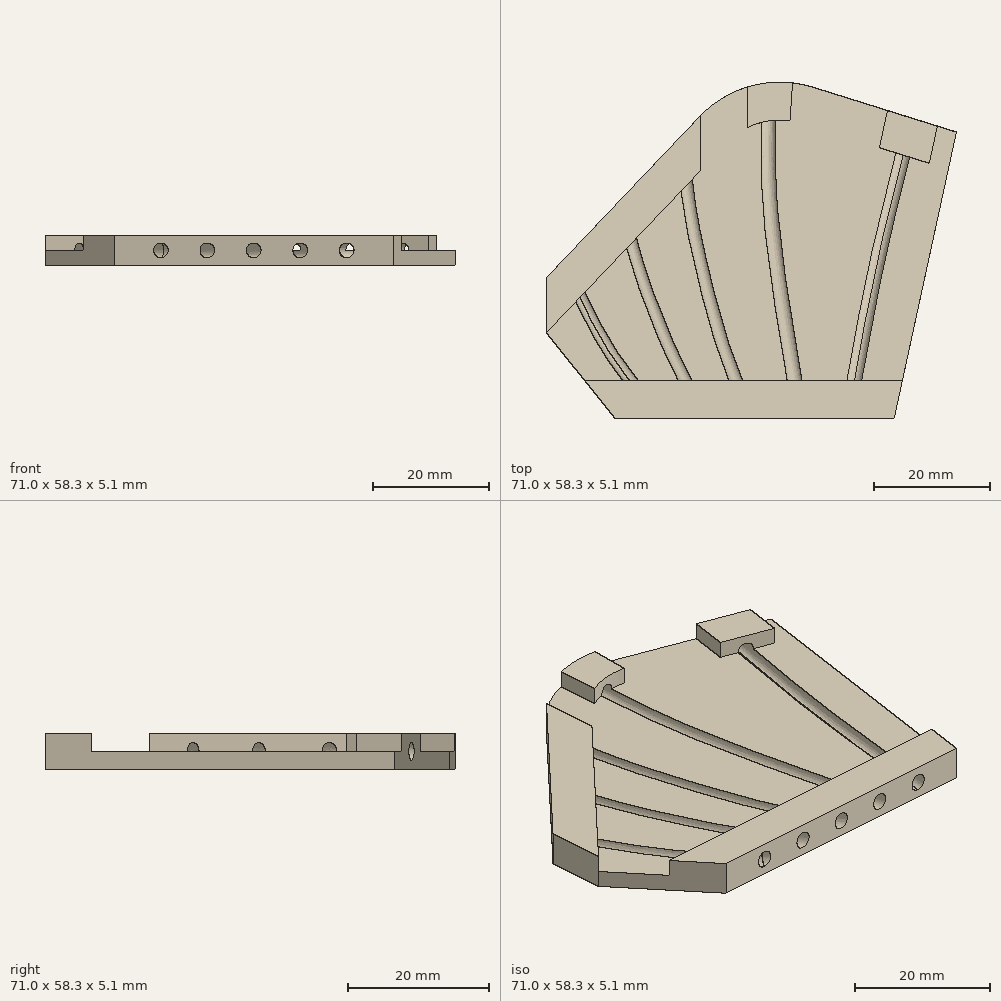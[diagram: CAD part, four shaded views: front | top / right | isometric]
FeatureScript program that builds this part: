
annotation { "Feature Type Name" : "Feature", "Feature Type Description" : "" }
export const myFeature = defineFeature(function(context is Context, id is Id, definition is map)
    precondition{}
    {
        {
            var Q0;
            Q0=qCreatedBy(makeId("Top.planeOp"),FACE);
            var sketch = newSketch(context, id + "F0", { "sketchPlane" : qUnion([Q0])});
            skLineSegment(sketch, "E0", {"start": v(0, 0) * mm, "end": v(48.26, 0) * mm});
            skSolve(sketch);
        }
        {
            var Q0;
            Q0=qCreatedBy(makeId("Top.planeOp"),FACE);
            var sketch = newSketch(context, id + "F1", { "sketchPlane" : qUnion([Q0])});
            skLineSegment(sketch, "E1", {"start": v(0, 0) * mm, "end": v(48.26, 0) * mm});
            skLineSegment(sketch, "E2", {"start": v(48.26, 0) * mm, "end": v(59.06, 49.64) * mm});
            skLineSegment(sketch, "E3", {"start": v(0, 0) * mm, "end": v(-11.94, 14.85) * mm});
            skLineSegment(sketch, "E4", {"start": v(-11.94, 14.85) * mm, "end": v(-11.94, 24.37) * mm});
            skLineSegment(sketch, "E5", {"start": v(-11.94, 24.37) * mm, "end": v(14.69, 52.37) * mm});
            skLineSegment(sketch, "E6", {"start": v(34.18, 57.42) * mm, "end": v(59.06, 49.64) * mm});
            skPoint(sketch, "E7.visualSharp", {"position": v(22.86, 60.96) * mm});
            skArc(sketch, "E7.filletArc", {"start": v(34.18, 57.42) * mm, "mid": v(23.71, 57.68) * mm, "end": v(14.69, 52.37) * mm});
            skSolve(sketch);
        }
        {
            var Q0;
            Q0 = qSketchRegion(id + "F1", true);
            extrude(context, id + "F2", {"entities" : qUnion([Q0]), "depth" : 2.54 * mm, "offsetDistance" : 25.4 * mm});
        }
        {
            var Q0;
            Q0=makeQuery(id+"F2.opExtrude","CAP_FACE",FACE,{"disambiguationData":[OSD([sQuery(id+"F1.wireOp",EDGE,"E1"),sQuery(id+"F1.wireOp",EDGE,"E2"),sQuery(id+"F1.wireOp",EDGE,"E3"),sQuery(id+"F1.wireOp",EDGE,"E4"),sQuery(id+"F1.wireOp",EDGE,"E5"),sQuery(id+"F1.wireOp",EDGE,"E6"),sQuery(id+"F1.wireOp",EDGE,"E7.filletArc")])],"isStart":false});
            var sketch = newSketch(context, id + "F3", { "sketchPlane" : qUnion([Q0])});
            skLineSegment(sketch, "E8", {"start": v(-11.94, 14.85) * mm, "end": v(14.69, 42.84) * mm});
            skLineSegment(sketch, "E9", {"start": v(14.69, 52.37) * mm, "end": v(14.69, 42.84) * mm});
            skLineSegment(sketch, "E10", {"start": v(49.69, 6.56) * mm, "end": v(-5.28, 6.56) * mm});
            skLineSegment(sketch, "E11.0", {"start": v(45.72, 46.93) * mm, "end": v(54.36, 44.23) * mm});
            skArc(sketch, "E11.1", {"start": v(30.23, 51.6) * mm, "mid": v(26.45, 51.56) * mm, "end": v(22.85, 50.38) * mm});
            skLineSegment(sketch, "E12", {"start": v(30.23, 51.6) * mm, "end": v(30.67, 58.16) * mm});
            skLineSegment(sketch, "E13", {"start": v(22.85, 50.38) * mm, "end": v(22.85, 57.44) * mm});
            skLineSegment(sketch, "E14", {"start": v(55.76, 50.67) * mm, "end": v(54.36, 44.23) * mm});
            skLineSegment(sketch, "E15", {"start": v(47.12, 53.37) * mm, "end": v(45.72, 46.93) * mm});
            skSolve(sketch);
        }
        {
            var Q0;
            Q0 = qSketchRegion(id + "F3", true);
            var Q1;
            Q1=makeQuery(id+"F3.imprint","IMPRINT",FACE,{"disambiguationData":[TD([[makeQuery(id+"F3.imprint","IMPRINT",EDGE,{"derivedFrom":sQuery(id+"F3.wireOp",EDGE,"E8")}),1.0]])]});
            var Q2;
            Q2=makeQuery(id+"F3.imprint","IMPRINT",FACE,{"disambiguationData":[TD([[makeQuery(id+"F3.imprint","IMPRINT",EDGE,{"derivedFrom":sQuery(id+"F3.wireOp",EDGE,"E11.1")}),-1.0]])]});
            var Q3;
            Q3=makeQuery(id+"F3.imprint","IMPRINT",FACE,{"disambiguationData":[TD([[makeQuery(id+"F3.imprint","IMPRINT",EDGE,{"derivedFrom":sQuery(id+"F3.wireOp",EDGE,"E11.0")}),1.0]])]});
            var Q4;
            {var subQ0=sQuery(id+"F3.wireOp",EDGE,"E10");Q4=makeQuery(id+"F3.imprint","IMPRINT",FACE,{"disambiguationData":[TD([[makeQuery(id+"F3.imprint","IMPRINT",EDGE,{"derivedFrom":subQ0}),1.0]])]});}
            extrude(context, id + "F4", {"entities" : qUnion([Q0, Q1, Q2, Q3, Q4]), "operationType" : NewBodyOperationType.ADD, "depth" : 2.54 * mm, "offsetDistance" : 25.4 * mm});
        }
        {
            var Q0;
            Q0=makeQuery(id+"F2.opExtrude","CAP_FACE",FACE,{"disambiguationData":[OSD([sQuery(id+"F1.wireOp",EDGE,"E1"),sQuery(id+"F1.wireOp",EDGE,"E2"),sQuery(id+"F1.wireOp",EDGE,"E3"),sQuery(id+"F1.wireOp",EDGE,"E4"),sQuery(id+"F1.wireOp",EDGE,"E5"),sQuery(id+"F1.wireOp",EDGE,"E6"),sQuery(id+"F1.wireOp",EDGE,"E7.filletArc")])],"isStart":false});
            var sketch = newSketch(context, id + "F5", { "sketchPlane" : qUnion([Q0])});
            skPoint(sketch, "E16", {"position": v(8.04, 0) * mm});
            skPoint(sketch, "E17.1.0.0", {"position": v(16.09, 0) * mm});
            skPoint(sketch, "E17.2.0.0", {"position": v(24.13, 0) * mm});
            skPoint(sketch, "E17.3.0.0", {"position": v(32.17, 0) * mm});
            skPoint(sketch, "E17.4.0.0", {"position": v(40.22, 0) * mm});
            skLineSegment(sketch, "E17.direction1", {"start": v(8.04, 0) * mm, "end": v(16.09, 0) * mm, "construction": true});
            skPoint(sketch, "E18", {"position": v(51.44, 52.02) * mm});
            skPoint(sketch, "E19.visualSharp", {"position": v(22.86, 60.96) * mm});
            skPoint(sketch, "E20", {"position": v(26.72, 58.2) * mm});
            skLineSegment(sketch, "E21", {"start": v(14.69, 52.37) * mm, "end": v(-11.94, 24.37) * mm});
            skPoint(sketch, "E22", {"position": v(1.37, 38.37) * mm});
            skPoint(sketch, "E23", {"position": v(11.88, 49.41) * mm});
            skPoint(sketch, "E24", {"position": v(-9.13, 27.33) * mm});
            skFitSpline(sketch, "E25", {"points": [v(51.44, 52.02) * mm, v(45.36, 27.29) * mm, v(40.22, 0) * mm], "startDerivative": vector(-13.01, -49.86) * mm, "endDerivative": vector(-9.46, -54.16) * mm});
            skFitSpline(sketch, "E26", {"points": [v(26.72, 58.2) * mm, v(26.72, 37.31) * mm, v(32.17, 0) * mm], "startDerivative": vector(-2.03, -45.53) * mm, "endDerivative": vector(12.23, -69.7) * mm});
            skFitSpline(sketch, "E27", {"points": [v(11.88, 49.41) * mm, v(15.75, 22.82) * mm, v(24.13, 0) * mm], "startDerivative": vector(-0.7, -55.32) * mm, "endDerivative": vector(25.48, -43.38) * mm});
            skFitSpline(sketch, "E28", {"points": [v(1.37, 38.37) * mm, v(6.4, 19.33) * mm, v(16.09, 0) * mm], "startDerivative": vector(3.78, -39.84) * mm, "endDerivative": vector(25.36, -36.93) * mm});
            skFitSpline(sketch, "E29", {"points": [v(-9.13, 27.33) * mm, v(-1.03, 11.48) * mm, v(8.04, 0) * mm], "startDerivative": vector(14.48, -31.8) * mm, "endDerivative": vector(19.95, -22.7) * mm});
            skSolve(sketch);
        }
        {
            var Q0;
            {var subQ0=sQuery(id+"F1.wireOp",EDGE,"E1");Q0=makeQuery(id+"F4.boolean.opBoolean","MERGE",FACE,{"derivedFrom":[makeQuery(id+"F2.opExtrude","SWEPT_FACE",FACE,{"disambiguationData":[OSD([subQ0])]}),makeQuery(id+"F4.opExtrude","SWEPT_FACE",FACE,{"disambiguationData":[OSD([subQ0])]})]});}
            var sketch = newSketch(context, id + "F6", { "sketchPlane" : qUnion([Q0])});
            skCircle(sketch, "E30", {"center": v(8.04, 2.54) * mm, "radius": 1.27 * mm});
            skPoint(sketch, "E30.centerSnap0", {"position": v(0, 2.54) * mm});
            skCircle(sketch, "E31.1.0.0", {"center": v(16.09, 2.54) * mm, "radius": 1.27 * mm});
            skCircle(sketch, "E31.2.0.0", {"center": v(24.13, 2.54) * mm, "radius": 1.27 * mm});
            skCircle(sketch, "E31.3.0.0", {"center": v(32.17, 2.54) * mm, "radius": 1.27 * mm});
            skCircle(sketch, "E31.4.0.0", {"center": v(40.22, 2.54) * mm, "radius": 1.27 * mm});
            skLineSegment(sketch, "E31.direction1", {"start": v(8.04, 2.54) * mm, "end": v(16.09, 2.54) * mm, "construction": true});
            skSolve(sketch);
        }
        {
            var Q0;
            Q0=makeQuery(id+"F6.imprint","IMPRINT",FACE,{"disambiguationData":[TD([[makeQuery(id+"F6.imprint","IMPRINT",EDGE,{"derivedFrom":sQuery(id+"F6.wireOp",EDGE,"E31.4.0.0")}),1.0]])]});
            var Q1;
            Q1=sQuery(id+"F5.wireOp",EDGE,"E25");
            sweep(context, id + "F7", {"operationType" : NewBodyOperationType.REMOVE, "profiles" : qUnion([Q0]), "path" : qUnion([Q1])});
        }
        {
            var Q0;
            Q0=makeQuery(id+"F6.imprint","IMPRINT",FACE,{"disambiguationData":[TD([[makeQuery(id+"F6.imprint","IMPRINT",EDGE,{"derivedFrom":sQuery(id+"F6.wireOp",EDGE,"E31.3.0.0")}),1.0]])]});
            var Q1;
            Q1=sQuery(id+"F5.wireOp",EDGE,"E26");
            sweep(context, id + "F8", {"operationType" : NewBodyOperationType.REMOVE, "profiles" : qUnion([Q0]), "path" : qUnion([Q1])});
        }
        {
            var Q0;
            Q0=makeQuery(id+"F6.imprint","IMPRINT",FACE,{"disambiguationData":[TD([[makeQuery(id+"F6.imprint","IMPRINT",EDGE,{"derivedFrom":sQuery(id+"F6.wireOp",EDGE,"E31.2.0.0")}),1.0]])]});
            var Q1;
            Q1=sQuery(id+"F5.wireOp",EDGE,"E27");
            sweep(context, id + "F9", {"operationType" : NewBodyOperationType.REMOVE, "profiles" : qUnion([Q0]), "path" : qUnion([Q1])});
        }
        {
            var Q0;
            Q0=makeQuery(id+"F6.imprint","IMPRINT",FACE,{"disambiguationData":[TD([[makeQuery(id+"F6.imprint","IMPRINT",EDGE,{"derivedFrom":sQuery(id+"F6.wireOp",EDGE,"E31.1.0.0")}),1.0]])]});
            var Q1;
            Q1=sQuery(id+"F5.wireOp",EDGE,"E28");
            sweep(context, id + "F10", {"operationType" : NewBodyOperationType.REMOVE, "profiles" : qUnion([Q0]), "path" : qUnion([Q1])});
        }
        {
            var Q0;
            Q0=makeQuery(id+"F6.imprint","IMPRINT",FACE,{"disambiguationData":[TD([[makeQuery(id+"F6.imprint","IMPRINT",EDGE,{"derivedFrom":sQuery(id+"F6.wireOp",EDGE,"E30")}),1.0]])]});
            var Q1;
            Q1=sQuery(id+"F6.wireOp",EDGE,"E30");
            var Q2;
            Q2=sQuery(id+"F5.wireOp",EDGE,"E29");
            sweep(context, id + "F11", {"operationType" : NewBodyOperationType.REMOVE, "profiles" : qUnion([Q0]), "surfaceProfiles" : qUnion([Q1]), "path" : qUnion([Q2])});
        }
        {
            var Q0;
            {var subQ0=sQuery(id+"F1.wireOp",EDGE,"E5");Q0=makeQuery(id+"F4.boolean.opBoolean","MERGE",FACE,{"derivedFrom":[makeQuery(id+"F2.opExtrude","SWEPT_FACE",FACE,{"disambiguationData":[OSD([subQ0])]}),makeQuery(id+"F4.opExtrude","SWEPT_FACE",FACE,{"disambiguationData":[OSD([subQ0])]})]});}
            var sketch = newSketch(context, id + "F12", { "sketchPlane" : qUnion([Q0])});
            skCircle(sketch, "E32", {"center": v(-44, 2.54) * mm, "radius": 1.27 * mm});
            skCircle(sketch, "E33", {"center": v(-28.75, 2.54) * mm, "radius": 1.27 * mm});
            skCircle(sketch, "E34", {"center": v(-13.51, 2.54) * mm, "radius": 1.27 * mm});
            skSolve(sketch);
        }
        {
            var Q0;
            {var subQ1=sQuery(id+"F6.wireOp",EDGE,"E31.2.0.0");var subQ2=sQuery(id+"F1.wireOp",EDGE,"E5");var subQ3=makeQuery(id+"F4.boolean.opBoolean","MERGE",FACE,{"derivedFrom":[makeQuery(id+"F2.opExtrude","SWEPT_FACE",FACE,{"disambiguationData":[OSD([subQ2])]}),makeQuery(id+"F4.opExtrude","SWEPT_FACE",FACE,{"disambiguationData":[OSD([subQ2])]})]});var subQ5=makeQuery(id+"F9.boolean.opBoolean","INTERSECT",EDGE,{"derivedFrom":[subQ3,makeQuery(id+"F9.opSweep","CAP_FACE",FACE,{"disambiguationData":[OSD([sQuery(id+"F5.wireOp",VERTEX,"E27.start"),subQ1])],"isStart":false})]});Q0=makeQuery(id+"F12.imprint","IMPRINT",FACE,{"disambiguationData":[TD([[makeQuery(id+"F12.imprint","IMPRINT",EDGE,{"derivedFrom":subQ5}),1.0]])]});}
            var Q1;
            Q1=sQuery(id+"F5.wireOp",EDGE,"E27");
            sweep(context, id + "F13", {"operationType" : NewBodyOperationType.REMOVE, "profiles" : qUnion([Q0]), "path" : qUnion([Q1])});
        }
        {
            var Q0;
            {var subQ1=sQuery(id+"F6.wireOp",EDGE,"E31.1.0.0");var subQ2=sQuery(id+"F1.wireOp",EDGE,"E5");var subQ3=makeQuery(id+"F4.boolean.opBoolean","MERGE",FACE,{"derivedFrom":[makeQuery(id+"F2.opExtrude","SWEPT_FACE",FACE,{"disambiguationData":[OSD([subQ2])]}),makeQuery(id+"F4.opExtrude","SWEPT_FACE",FACE,{"disambiguationData":[OSD([subQ2])]})]});var subQ5=makeQuery(id+"F10.boolean.opBoolean","INTERSECT",EDGE,{"derivedFrom":[subQ3,makeQuery(id+"F10.opSweep","CAP_FACE",FACE,{"disambiguationData":[OSD([sQuery(id+"F5.wireOp",VERTEX,"E28.start"),subQ1])],"isStart":false})]});Q0=makeQuery(id+"F12.imprint","IMPRINT",FACE,{"disambiguationData":[TD([[makeQuery(id+"F12.imprint","IMPRINT",EDGE,{"derivedFrom":subQ5}),1.0]])]});}
            var Q1;
            Q1=sQuery(id+"F5.wireOp",EDGE,"E28");
            sweep(context, id + "F14", {"operationType" : NewBodyOperationType.REMOVE, "profiles" : qUnion([Q0]), "path" : qUnion([Q1])});
        }
        {
            var Q0;
            {var subQ1=sQuery(id+"F6.wireOp",EDGE,"E30");var subQ2=sQuery(id+"F1.wireOp",EDGE,"E5");var subQ3=makeQuery(id+"F4.boolean.opBoolean","MERGE",FACE,{"derivedFrom":[makeQuery(id+"F2.opExtrude","SWEPT_FACE",FACE,{"disambiguationData":[OSD([subQ2])]}),makeQuery(id+"F4.opExtrude","SWEPT_FACE",FACE,{"disambiguationData":[OSD([subQ2])]})]});var subQ5=makeQuery(id+"F11.boolean.opBoolean","INTERSECT",EDGE,{"derivedFrom":[subQ3,makeQuery(id+"F11.opSweep","CAP_FACE",FACE,{"disambiguationData":[OSD([sQuery(id+"F5.wireOp",VERTEX,"E29.start"),subQ1])],"isStart":false})]});Q0=makeQuery(id+"F12.imprint","IMPRINT",FACE,{"disambiguationData":[TD([[makeQuery(id+"F12.imprint","IMPRINT",EDGE,{"derivedFrom":subQ5}),1.0]])]});}
            var Q1;
            Q1=sQuery(id+"F5.wireOp",EDGE,"E29");
            sweep(context, id + "F15", {"operationType" : NewBodyOperationType.REMOVE, "profiles" : qUnion([Q0]), "path" : qUnion([Q1])});
        }
        {
            var Q0;
            Q0=makeQuery(id+"F8.boolean.opBoolean","COPY",FACE,{"derivedFrom":makeQuery(id+"F8.opSweep","CAP_FACE",FACE,{"disambiguationData":[OSD([sQuery(id+"F5.wireOp",VERTEX,"E26.start"),sQuery(id+"F6.wireOp",EDGE,"E31.3.0.0")])],"isStart":false})});
            var sketch = newSketch(context, id + "F16", { "sketchPlane" : qUnion([Q0])});
            skCircle(sketch, "E35", {"center": v(13.49, 2.54) * mm, "radius": 1.27 * mm});
            skSolve(sketch);
        }
        {
            var Q0;
            Q0 = qSketchRegion(id + "F16", true);
            extrude(context, id + "F17", {"entities" : qUnion([Q0]), "operationType" : NewBodyOperationType.REMOVE, "endBound" : BoundingType.THROUGH_ALL, "oppositeDirection" : true, "depth" : 25.4 * mm, "offsetDistance" : 25.4 * mm});
        }
        {
            var Q0;
            {var subQ0=sQuery(id+"F1.wireOp",EDGE,"E6");Q0=makeQuery(id+"F4.boolean.opBoolean","MERGE",FACE,{"derivedFrom":[makeQuery(id+"F2.opExtrude","SWEPT_FACE",FACE,{"disambiguationData":[OSD([subQ0])]}),makeQuery(id+"F4.opExtrude","SWEPT_FACE",FACE,{"disambiguationData":[OSD([subQ0])]})]});}
            var sketch = newSketch(context, id + "F18", { "sketchPlane" : qUnion([Q0])});
            skCircle(sketch, "E36", {"center": v(-33.57, 2.54) * mm, "radius": 1.27 * mm});
            skSolve(sketch);
        }
        {
            var Q0;
            {var subQ1=sQuery(id+"F6.wireOp",EDGE,"E31.4.0.0");var subQ2=sQuery(id+"F1.wireOp",EDGE,"E6");var subQ3=makeQuery(id+"F4.boolean.opBoolean","MERGE",FACE,{"derivedFrom":[makeQuery(id+"F2.opExtrude","SWEPT_FACE",FACE,{"disambiguationData":[OSD([subQ2])]}),makeQuery(id+"F4.opExtrude","SWEPT_FACE",FACE,{"disambiguationData":[OSD([subQ2])]})]});var subQ5=makeQuery(id+"F7.boolean.opBoolean","INTERSECT",EDGE,{"derivedFrom":[subQ3,makeQuery(id+"F7.opSweep","CAP_FACE",FACE,{"disambiguationData":[OSD([sQuery(id+"F5.wireOp",VERTEX,"E25.start"),subQ1])],"isStart":false})]});Q0=makeQuery(id+"F18.imprint","IMPRINT",FACE,{"disambiguationData":[TD([[makeQuery(id+"F18.imprint","IMPRINT",EDGE,{"derivedFrom":subQ5}),1.0]])]});}
            var Q1;
            Q1=sQuery(id+"F5.wireOp",EDGE,"E25");
            sweep(context, id + "F19", {"operationType" : NewBodyOperationType.REMOVE, "profiles" : qUnion([Q0]), "path" : qUnion([Q1])});
        }
    });
